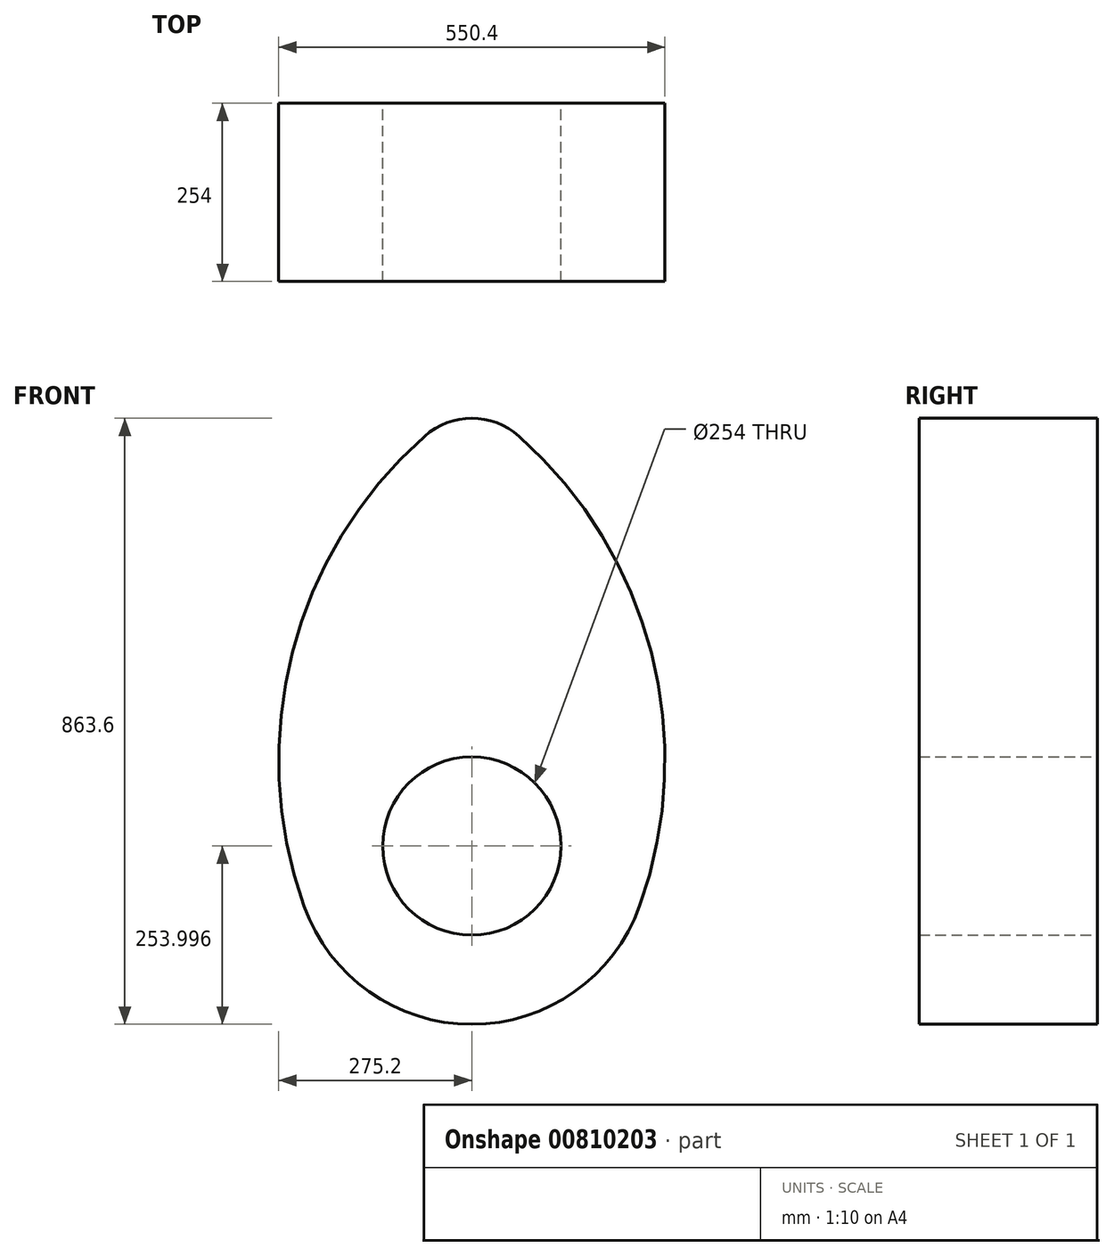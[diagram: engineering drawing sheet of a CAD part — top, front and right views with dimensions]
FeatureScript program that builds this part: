
annotation { "Feature Type Name" : "Feature", "Feature Type Description" : "" }
export const myFeature = defineFeature(function(context is Context, id is Id, definition is map)
    precondition{}
    {
        {
            var Q0;
            Q0=qCreatedBy(makeId("Front.planeOp"),FACE);
            var sketch = newSketch(context, id + "F0", { "sketchPlane" : qUnion([Q0])});
            skCircle(sketch, "E0", {"center": v(0, -96) * mm, "radius": 127 * mm});
            skArc(sketch, "E1", {"start": v(-239.17, -181.51) * mm, "mid": v(0, -350) * mm, "end": v(239.17, -181.51) * mm});
            skArc(sketch, "E2", {"start": v(67.38, 488.05) * mm, "mid": v(0, 513.6) * mm, "end": v(-67.38, 488.05) * mm});
            skArc(sketch, "E3", {"start": v(-67.38, 488.05) * mm, "mid": v(-255.84, 179.58) * mm, "end": v(-239.17, -181.51) * mm});
            skArc(sketch, "E4.MirrorCS", {"start": v(67.38, 488.05) * mm, "mid": v(255.84, 179.58) * mm, "end": v(239.17, -181.51) * mm});
            skSolve(sketch);
        }
        {
            var Q0;
            Q0=makeQuery(id+"F0.imprint","IMPRINT",FACE,{"disambiguationData":[TD([[makeQuery(id+"F0.imprint","IMPRINT",EDGE,{"derivedFrom":sQuery(id+"F0.wireOp",EDGE,"E0")}),-1.0]])]});
            extrude(context, id + "F1", {"entities" : qUnion([Q0]), "depth" : 254 * mm, "offsetDistance" : 25.4 * mm});
        }
    });
